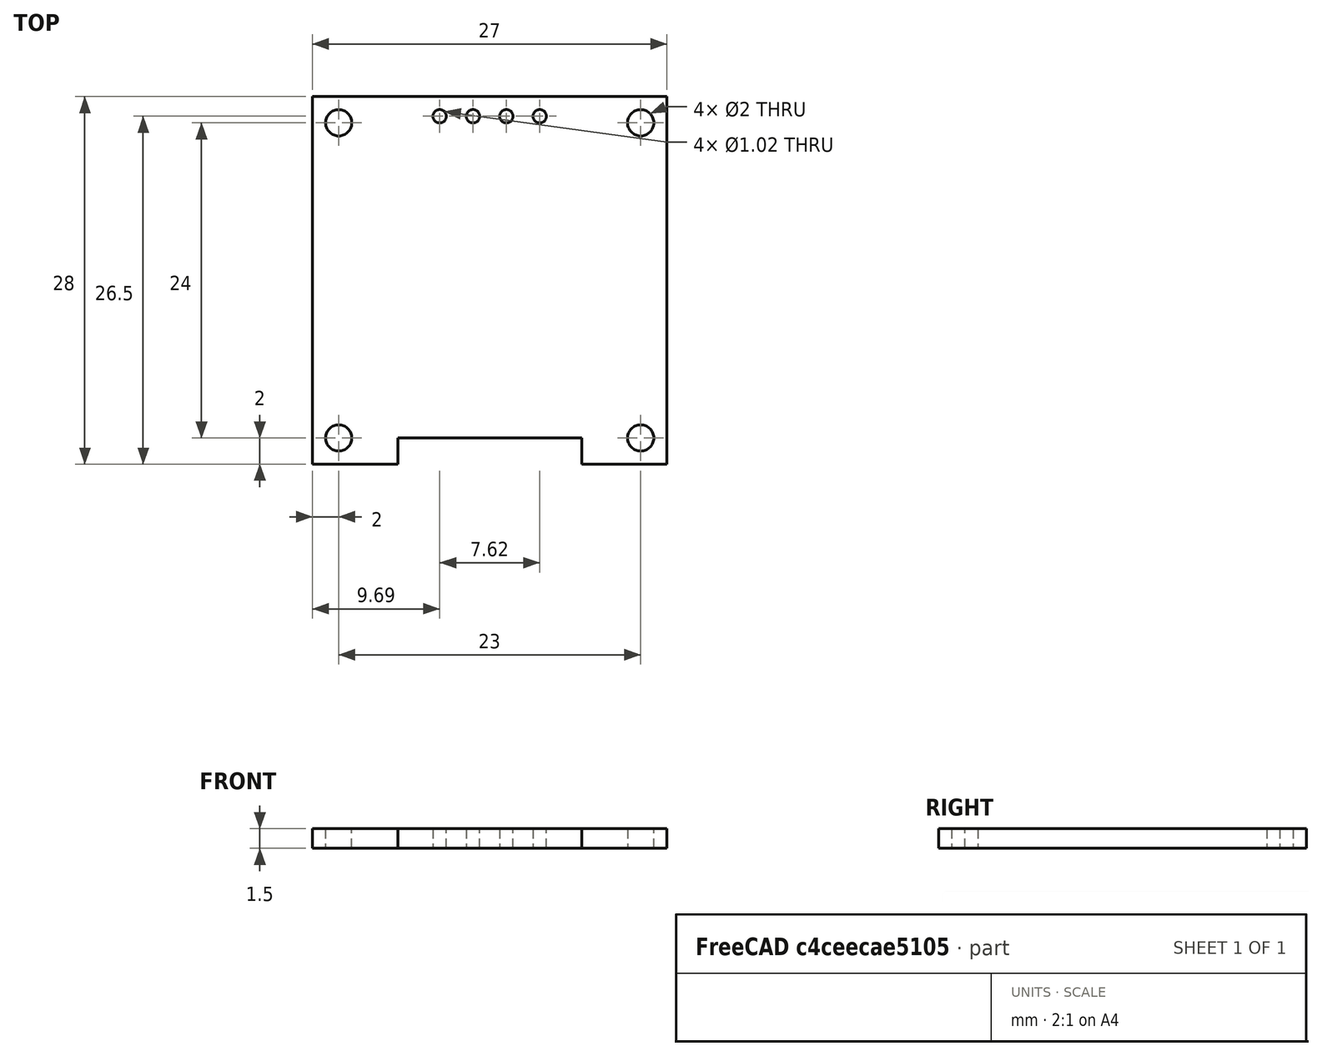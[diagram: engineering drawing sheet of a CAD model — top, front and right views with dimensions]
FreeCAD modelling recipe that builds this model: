
FCSTD DOCUMENT  (FreeCAD 0.19R24276 (Git))
Label: PCB
License: All rights reserved
LicenseURL: http://en.wikipedia.org/wiki/All_rights_reserved
objects: Sketcher::SketchObject×1, PartDesign::Pad×1, PartDesign::Body×1
note: 4 computed .brp shape members not serialized (recipe doc carries the construction recipe); baked Part::Feature solids carry a one-line shape summary decoded from their .brp

FEATURE [Sketcher::SketchObject] Sketch
  FullyConstrained = true
  MapMode = 5
  Support = -> [XY_Plane]
  sketch-geometry (16):
    g0: LineSegment StartX=-13.5 StartY=14 StartZ=0 EndX=13.5 EndY=14 EndZ=0
    g1: LineSegment StartX=13.5 StartY=14 StartZ=0 EndX=13.5 EndY=-14 EndZ=0
    g2: LineSegment StartX=-13.5 StartY=-14 StartZ=0 EndX=-13.5 EndY=14 EndZ=0
    g3: Circle CenterX=-11.5 CenterY=12 CenterZ=0 NormalX=0 NormalY=0 NormalZ=1 AngleXU=0 Radius=1
    g4: Circle CenterX=11.5 CenterY=12 CenterZ=0 NormalX=0 NormalY=0 NormalZ=1 AngleXU=0 Radius=1
    g5: Circle CenterX=-11.5 CenterY=-12 CenterZ=0 NormalX=0 NormalY=0 NormalZ=1 AngleXU=0 Radius=1
    g6: Circle CenterX=11.5 CenterY=-12 CenterZ=0 NormalX=0 NormalY=0 NormalZ=1 AngleXU=0 Radius=1
    g7: Circle CenterX=-3.81 CenterY=12.5 CenterZ=0 NormalX=0 NormalY=0 NormalZ=1 AngleXU=0 Radius=0.51
    g8: Circle CenterX=-1.27 CenterY=12.5 CenterZ=0 NormalX=0 NormalY=0 NormalZ=1 AngleXU=0 Radius=0.51
    g9: Circle CenterX=1.27 CenterY=12.5 CenterZ=0 NormalX=0 NormalY=0 NormalZ=1 AngleXU=0 Radius=0.51
    g10: Circle CenterX=3.81 CenterY=12.5 CenterZ=0 NormalX=0 NormalY=0 NormalZ=1 AngleXU=0 Radius=0.51
    g11: LineSegment StartX=7 StartY=-14 StartZ=0 EndX=7 EndY=-12 EndZ=0
    g12: LineSegment StartX=7 StartY=-12 StartZ=0 EndX=-7 EndY=-12 EndZ=0
    g13: LineSegment StartX=-7 StartY=-12 StartZ=0 EndX=-7 EndY=-14 EndZ=0
    g14: LineSegment StartX=-13.5 StartY=-14 StartZ=0 EndX=-7 EndY=-14 EndZ=0
    g15: LineSegment StartX=7 StartY=-14 StartZ=0 EndX=13.5 EndY=-14 EndZ=0
  constraints (48):
    c: Coincident(g0,g1)
    c: Coincident(g2,g0)
    c: Horizontal(g0)
    c: Vertical(g1)
    c: Vertical(g2)
    c: DistanceX(g0,g0) = 27
    c: DistanceY(g1,g1) = 28
    c: DistanceX(g0,g-1) = 13.5
    c: DistanceY(g-1,g0) = 14
    c: Diameter(g6) = 2
    c: Equal(g6,g5)
    c: Equal(g6,g3)
    c: Equal(g6,g4)
    c: DistanceY(g3,g0) = 2
    c: DistanceX(g0,g3) = 2
    c: DistanceY(g4,g0) = 2
    c: DistanceX(g4,g0) = 2
    c: DistanceX(g6,g1) = 2
    c: DistanceY(g1,g6) = 2
    c: DistanceY(g2,g5) = 2
    c: DistanceX(g2,g5) = 2
    c: Horizontal(g7,g8)
    c: Horizontal(g8,g9)
    c: Horizontal(g9,g10)
    c: DistanceX(g7,g8) = 2.54
    c: DistanceX(g8,g9) = 2.54
    c: DistanceX(g9,g10) = 2.54
    c: Diameter(g7) = 1.02
    c: Equal(g7,g8)
    c: Equal(g7,g9)
    c: Equal(g7,g10)
    c: DistanceX(g8,g-1) = 1.27
    c: DistanceY(g7,g0) = 1.5
    c: Coincident(g11,g12)
    c: Coincident(g12,g13)
    c: Horizontal(g12)
    c: Vertical(g11)
    c: Vertical(g13)
    c: Coincident(g14,g2)
    c: Coincident(g14,g13)
    c: Horizontal(g14)
    c: Coincident(g15,g11)
    c: Coincident(g15,g1)
    c: Horizontal(g15)
    c: Equal(g15,g14)
    c: DistanceY(g13,g13) = 2
    c: DistanceX(g12,g12) = 14
    c: Equal(g13,g11)
FEATURE [PartDesign::Pad] Pad
  Direction = (1,1,1)
  Length = 1.5
  Length2 = 100
  Profile = -> Sketch
  Type = 0
FEATURE [PartDesign::Body] Body
  Group = -> [Sketch,Pad]
  Origin = -> Origin
  Tip = -> Pad
